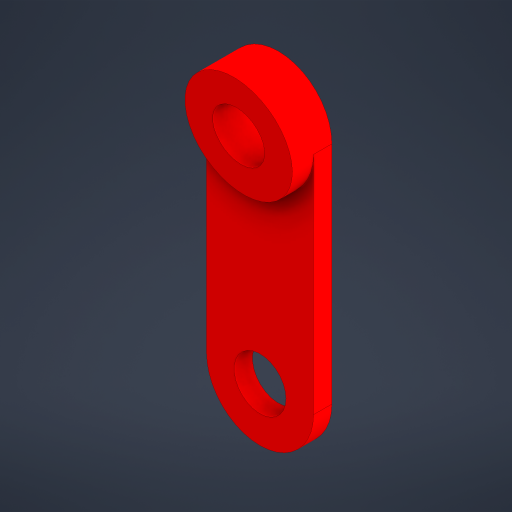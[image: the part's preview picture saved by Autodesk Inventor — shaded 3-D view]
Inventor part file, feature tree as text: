
AUTODESK INVENTOR PART (.ipt)
format: ipt  version: 2024 (Build 280153000, 153)  size: 236,032 bytes
history: native  units: mm
features: extrude x5, projected_geometry x5, sketch x3, other x1
ambient origin geometry x8: Origin, YZ Plane, XZ Plane, XY Plane, X Axis, Y Axis, Z Axis, Center Point
bodies: Body1 (feature_tree)
feature tree (14):
  other  "Těleso1"
  sketch  "Náčrt1"
  extrude  "Vysunutí1"  Depth=14.75mm
  extrude  "Vysunutí2"  Depth=3.5mm
  sketch  "Náčrt4"
  extrude  "Vysunutí3"  Depth=3.4mm
  extrude  "Vysunutí4"  Depth=1.2mm TaperAngle=0.0deg
  extrude  "Vysunutí5"  Depth=2.6mm TaperAngle=0.0deg
  projected_geometry  "Promítnutá smyčka1"
  sketch  "Náčrt5"
  projected_geometry  "Promítnutá smyčka2"
  projected_geometry  "Promítnutá smyčka3"
  projected_geometry  "Promítnutá smyčka4"
  projected_geometry  "Promítnutá smyčka5"
